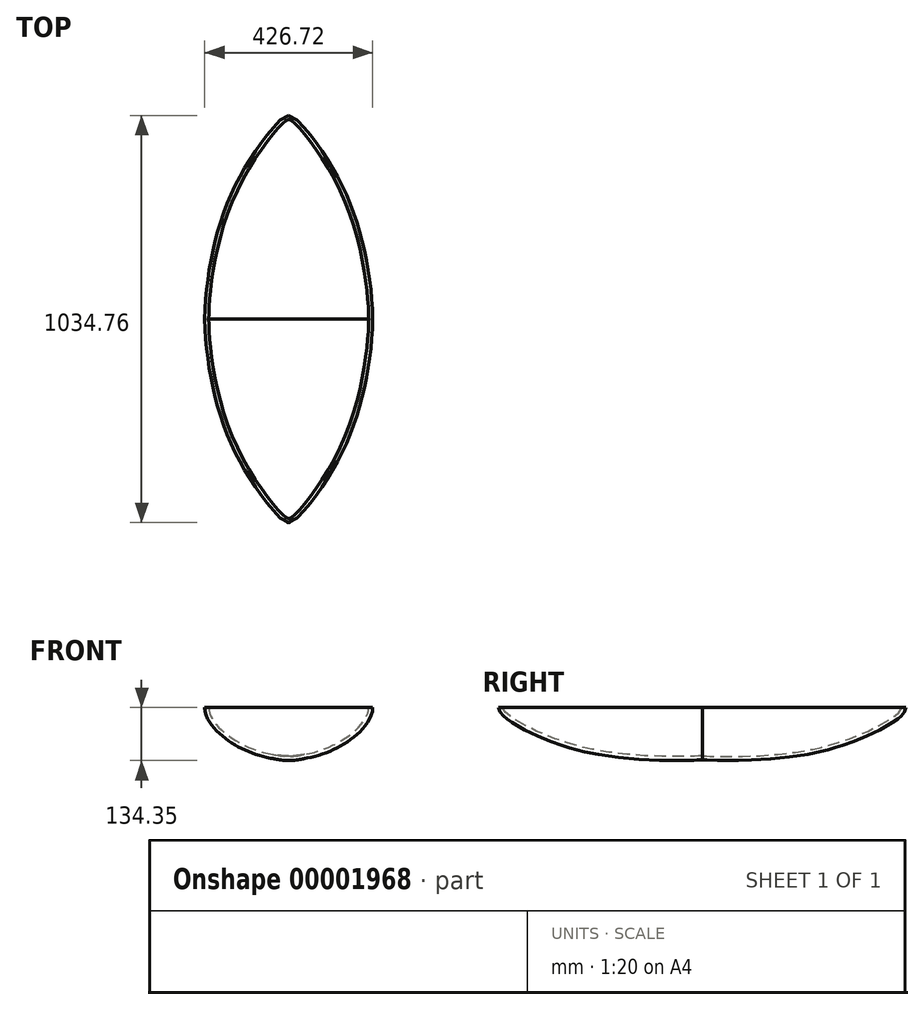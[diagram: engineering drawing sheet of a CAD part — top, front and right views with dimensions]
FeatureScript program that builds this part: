
annotation { "Feature Type Name" : "Feature", "Feature Type Description" : "" }
export const myFeature = defineFeature(function(context is Context, id is Id, definition is map)
    precondition{}
    {
        {
            var Q0;
            Q0=qCreatedBy(makeId("Front.planeOp"),FACE);
            var sketch = newSketch(context, id + "F0", { "sketchPlane" : qUnion([Q0])});
            skLineSegment(sketch, "E0.bottom", {"start": v(203.2, -50.8) * mm, "end": v(-203.2, -50.8) * mm, "construction": true});
            skLineSegment(sketch, "E0.top", {"start": v(203.2, 0) * mm, "end": v(-203.2, 0) * mm});
            skLineSegment(sketch, "E0.left", {"start": v(203.2, -50.8) * mm, "end": v(203.2, 0) * mm, "construction": true});
            skLineSegment(sketch, "E0.right", {"start": v(-203.2, -50.8) * mm, "end": v(-203.2, 0) * mm, "construction": true});
            skPoint(sketch, "E0.middle", {"position": v(0, -25.4) * mm});
            skLineSegment(sketch, "E1", {"start": v(0, 0) * mm, "end": v(0, -122.72) * mm, "construction": true});
            skFitSpline(sketch, "E2", {"points": [v(-203.2, 0) * mm, v(0, -122.72) * mm, v(203.2, 0) * mm], "startDerivative": vector(0, -304.8) * mm, "endDerivative": vector(0, 304.8) * mm});
            skSolve(sketch);
        }
        {
            var Q0;
            Q0=qCreatedBy(makeId("Top.planeOp"),FACE);
            var sketch = newSketch(context, id + "F1", { "sketchPlane" : qUnion([Q0])});
            skLineSegment(sketch, "E3", {"start": v(0, 0) * mm, "end": v(0, -507.22) * mm, "construction": true});
            skSolve(sketch);
        }
        {
            var Q0;
            Q0=qCreatedBy(makeId("Right.planeOp"),FACE);
            var sketch = newSketch(context, id + "F2", { "sketchPlane" : qUnion([Q0])});
            skFitSpline(sketch, "E4", {"points": [v(0, -122.72) * mm, v(-291.98, -103.16) * mm, v(-507.22, 0) * mm], "startDerivative": vector(-70.43, 0) * mm, "endDerivative": vector(0, 122.55) * mm});
            skSolve(sketch);
        }
        {
            var Q0;
            Q0=qCreatedBy(makeId("Top.planeOp"),FACE);
            var sketch = newSketch(context, id + "F3", { "sketchPlane" : qUnion([Q0])});
            skFitSpline(sketch, "E5", {"points": [v(203.2, 0) * mm, v(139.21, -307.38) * mm, v(0, -507.22) * mm], "startDerivative": vector(0, -286.85) * mm, "endDerivative": vector(-93.07, 0) * mm});
            skFitSpline(sketch, "E6.MirrorCS", {"points": [v(-203.2, 0) * mm, v(-139.21, -307.38) * mm, v(0, -507.22) * mm], "startDerivative": vector(0, -286.85) * mm, "endDerivative": vector(93.07, 0) * mm});
            skLineSegment(sketch, "E7", {"start": v(-203.2, 0) * mm, "end": v(203.2, 0) * mm, "construction": true});
            skSolve(sketch);
        }
        {
            var Q0;
            Q0=makeQuery(id+"F0.imprint","IMPRINT",FACE,{"disambiguationData":[TD([[makeQuery(id+"F0.imprint","IMPRINT",EDGE,{"derivedFrom":sQuery(id+"F0.wireOp",EDGE,"E0.top")}),1.0]])]});
            var Q1;
            Q1=sQuery(id+"F1.wireOp",VERTEX,"E3.end");
            var Q2;
            Q2=sQuery(id+"F3.wireOp",EDGE,"E5");
            var Q3;
            Q3=sQuery(id+"F2.wireOp",EDGE,"E4");
            var Q4;
            Q4=sQuery(id+"F3.wireOp",EDGE,"E6.MirrorCS");
            loft(context, id + "F4", {"addGuides" : true, "sheetProfilesArray" : [{ "sheetProfileEntities" : qUnion([Q0]) }, { "sheetProfileEntities" : qUnion([Q1]) }], "guidesArray" : [{ "guideEntities" : qUnion([Q2]), "guideDerivativeType" : LoftGuideDerivativeType.DEFAULT, "guideDerivativeMagnitude" : 1 }, { "guideEntities" : qUnion([Q3]), "guideDerivativeType" : LoftGuideDerivativeType.DEFAULT, "guideDerivativeMagnitude" : 1 }, { "guideEntities" : qUnion([Q4]), "guideDerivativeType" : LoftGuideDerivativeType.DEFAULT, "guideDerivativeMagnitude" : 1 }]});
        }
        {
            var Q0;
            Q0=makeQuery(id+"F4.opLoft","SWEPT_BODY",BODY,{"disambiguationData":[OSD([makeQuery(id+"F0.imprint","IMPRINT",FACE,{"disambiguationData":[TD([[makeQuery(id+"F0.imprint","IMPRINT",EDGE,{"derivedFrom":sQuery(id+"F0.wireOp",EDGE,"E0.top")}),1.0]])]}),sQuery(id+"F1.wireOp",VERTEX,"E3.end"),sQuery(id+"F2.wireOp",EDGE,"E4"),sQuery(id+"F3.wireOp",EDGE,"E5"),sQuery(id+"F3.wireOp",EDGE,"E6.MirrorCS")])]});
            var Q1;
            Q1=makeQuery(id+"F0.imprint","IMPRINT",FACE,{"disambiguationData":[TD([[makeQuery(id+"F0.imprint","IMPRINT",EDGE,{"derivedFrom":sQuery(id+"F0.wireOp",EDGE,"E0.top")}),1.0]])]});
            mirror(context, id + "F5", {"operationType" : NewBodyOperationType.ADD, "entities" : qUnion([Q0]), "mirrorPlane" : qUnion([Q1])});
        }
        {
            var Q0;
            {var subQ0=makeQuery(id+"F4.opLoft","SWEPT_FACE",FACE,{"disambiguationData":[OSD([sQuery(id+"F0.wireOp",EDGE,"E0.top"),sQuery(id+"F0.wireOp",EDGE,"E2"),sQuery(id+"F3.wireOp",EDGE,"E5"),sQuery(id+"F3.wireOp",EDGE,"E6.MirrorCS")])]});Q0=makeQuery(id+"F5.boolean.opBoolean","MERGE",FACE,{"derivedFrom":[subQ0,makeQuery(id+"F5.opPattern","COPY",FACE,{"derivedFrom":subQ0,"instanceName":"1"})]});}
            shell(context, id + "F6", {"entities" : qUnion([Q0]), "thickness" : 10.16 * mm, "oppositeDirection" : true});
        }
    });
